# Revit family: High pivot window FAKRO FDY-V_U Duet proSky
name_source: partatom
category: Okna
revit_build: Autodesk Revit 2015 (Build: 20140606_1530(x64)
units: mm (PartAtom-declared; Revit-internal decimal feet)

## types (8) — shared parameters
Apron Material = Fakro - aluminium RAL7022
Bimobject Category = Windows - Roof Windows
CSI MasterFormat 2016 Code = 08 60 00
CSI MasterFormat 2016 Title = Roof Windows and Skylights
CSI UniFormat II Code = B3020
CSI UniFormat II Title = Roof Openings
Glazing = Fakro – Glass
Handle Material = Fakro – handle
IFC Classification = Window
Kod zespołu = B3020110
Material External = Fakro - aluminium RAL7022
Material Internal = Fakro - frame - pinewood - RAL 9010
Model = FDY-V/U U3 Duet proSky
NBS Reference = 59-72
NBS Reference Description = Roof Window Units
Opis = High pivot window
Producent = FAKRO
UNSPC Category = Roofing accessories
UNSPC Code = 301516
URL = www.fakro.com
UV radiation EN 14351-1:2006+A1:2010 = 0.26
Uniclass 1.4 Code = JL11
Uniclass 1.4 Description = Rooflights/Roof windows
Uniclass 2.0 Code = PR-59-72
Uniclass 2.0 Description = Roof Window Units
Uniclass 2015 Code = Pr_30_59_72_77
Uniclass 2015 Title = Skylights
air inlet = V40P
air inlet efficiency - 10Pa = 27 m³/h
air permeability class EN 14351-1:2006+A1:2010 = 3
colour = NCS S0502-Y (near to RAL 9010)
glass structure = 4H-16-4T
glazing U-value [W/m2K] EN 14351-1:2006+A1:2010 = 1
impact resistance class EN 14351-1:2006+A1:2010 = 3
light transmittance factor tv EN 14351-1:2006+A1:2010 = 0.7
material = pinewood
opening method = pivot
operation mode = manual
reaction to fire EN 14351-1:2006+A1:2010 = D-s2.d2
resistance to snow load EN 14351-1:2006+A1:2010 = 4H-16-4
resistance to wind load EN 14351-1:2006+A1:2010 = C5
roof angle = 25-65
solar factor [ g] EN 14351-1:2006+A1:2010 = 0.53
watertightness / unshielded (A) EN 14351-1:2006+A1:2010 = E900
window acoustic performance Rw [dB] EN 14351-1:2006+A1:2010 = 32(-1;-5)
window heat transfer coefficient Uw [W/m2K] EN 14351-1:2006+A1:2010 = 1.3

## per-type parameters (varying)
| type | Obj Type | Parametr A | Szerokość | Wysokość | frame area | glass perimeter | glazing area | window internal area | window perimeter | window weight |
| FAKRO FDY-V/U U3 Duet proSky - CA - 78x186 | 1 mm  [stored 0.00328084 ft] | 1419 mm  [stored 4.65551 ft] | 777 mm  [stored 2.54921 ft] | 1861 mm  [stored 6.10564 ft] | 0.54 m² | 5798 mm | 0.91 m² | 1.19 m² | 5276 mm  [stored 17.3097 ft] | 55.00 kg |
| FAKRO FDY-V/U U3 Duet proSky - CB - 78x206 | 2 mm  [stored 0.00656168 ft] | 1617 mm  [stored 5.30512 ft] | 777 mm  [stored 2.54921 ft] | 2061 mm  [stored 6.76181 ft] | 0.57 m² | 6198 mm | 1.03 m² | 1.33 m² | 5676 mm  [stored 18.622 ft] | 60.00 kg |
| FAKRO FDY-V/U U3 Duet proSky - CC - 78x235 | 3 mm  [stored 0.00984252 ft] | 1617 mm  [stored 5.30512 ft] | 777 mm  [stored 2.54921 ft] | 2345 mm  [stored 7.69357 ft] | 0.62 m² | 6766 mm  [stored 22.1982 ft] | 1.2 m² | 1.52 m² | 6244 mm  [stored 20.4856 ft] | 66.00 kg |
| FAKRO FDY-V/U U3 Duet proSky - CD - 78x255 | 4 mm  [stored 0.0131234 ft] | 1617 mm  [stored 5.30512 ft] | 777 mm  [stored 2.54921 ft] | 2545 mm  [stored 8.34974 ft] | 0.66 m² | 7166 mm | 1.32 m² | 1.8 m² | 6644 mm  [stored 21.7979 ft] | 70.00 kg |
| FAKRO FDY-V/U U3 Duet proSky - DA - 94x186 | 5 mm  [stored 0.0164042 ft] | 1419 mm  [stored 4.65551 ft] | 937 mm  [stored 3.07415 ft] | 1861 mm  [stored 6.10564 ft] | 0.59 m² | 6438 mm  [stored 21.122 ft] | 1.15 m² | 1.46 m² | 5596 mm  [stored 18.3596 ft] | 65.00 kg |
| FAKRO FDY-V/U U3 Duet proSky - DB - 94x206 | 6 mm  [stored 0.019685 ft] | 1617 mm  [stored 5.30512 ft] | 937 mm  [stored 3.07415 ft] | 2061 mm  [stored 6.76181 ft] | 0.63 m² | 6838 mm  [stored 22.4344 ft] | 1.3 m² | 1.63 m² | 5996 mm  [stored 19.6719 ft] | 68.00 kg |
| FAKRO FDY-V/U U3 Duet proSky - DC - 94x235 | 7 mm  [stored 0.0229659 ft] | 1617 mm  [stored 5.30512 ft] | 937 mm  [stored 3.07415 ft] | 2345 mm  [stored 7.69357 ft] | 0.68 m² | 7406 mm  [stored 24.2979 ft] | 1.52 m² | 1.87 m² | 6564 mm  [stored 21.5354 ft] | 77.00 kg |
| FAKRO FDY-V/U U3 Duet proSky - DD - 94x255 | 8 mm  [stored 0.0262467 ft] | 1617 mm  [stored 5.30512 ft] | 937 mm  [stored 3.07415 ft] | 2545 mm  [stored 8.34974 ft] | 0.71 m² | 7806 mm | 1.67 m² | 2.04 m² | 6964 mm  [stored 22.8478 ft] | 83.00 kg |

note: [stored X ft] marks values corroborated as IEEE doubles in the binary element streams (Revit-internal decimal feet)

## geometry (parser evidence)
native form markers: Sweep x3
no freeform markers — native parametric forms only
